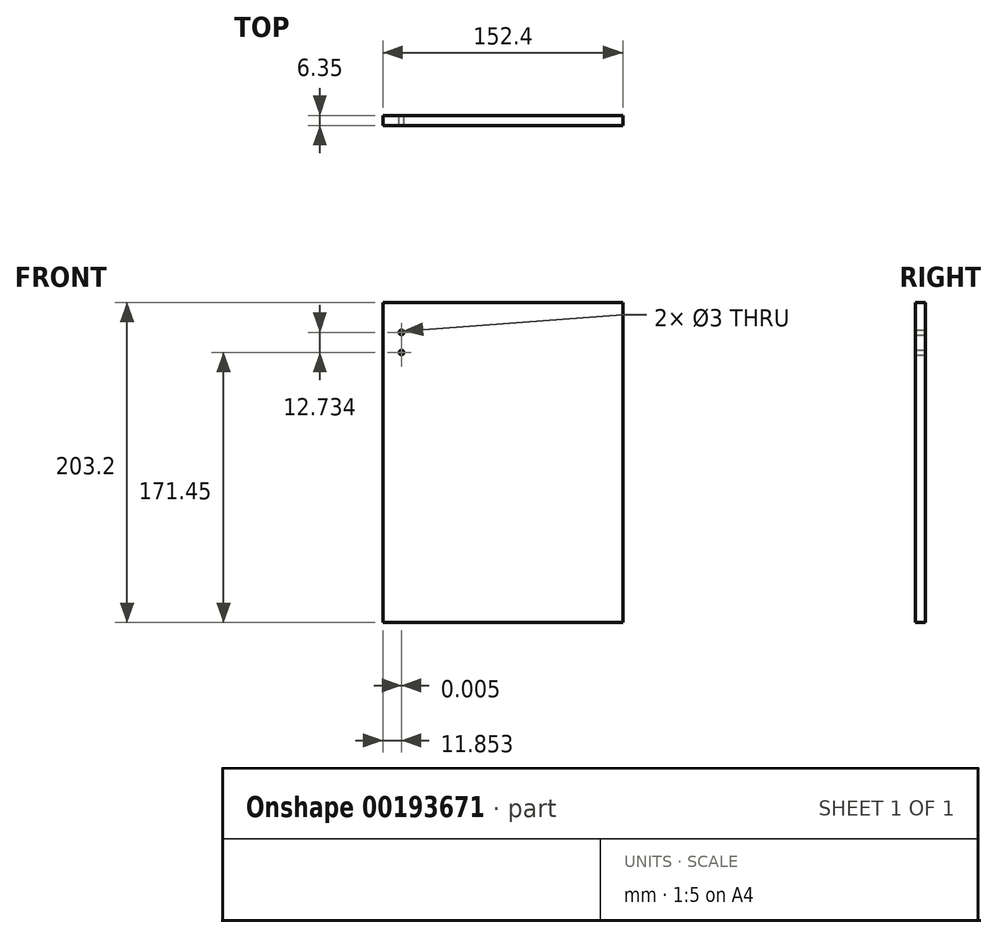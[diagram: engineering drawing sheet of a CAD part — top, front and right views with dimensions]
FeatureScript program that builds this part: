
annotation { "Feature Type Name" : "Feature", "Feature Type Description" : "" }
export const myFeature = defineFeature(function(context is Context, id is Id, definition is map)
    precondition{}
    {
        {
            var Q0;
            Q0=qCreatedBy(makeId("Front.planeOp"),FACE);
            var sketch = newSketch(context, id + "F0", { "sketchPlane" : qUnion([Q0])});
            skLineSegment(sketch, "E0.bottom", {"start": v(76.2, -101.6) * mm, "end": v(-76.2, -101.6) * mm});
            skLineSegment(sketch, "E0.top", {"start": v(76.2, 101.6) * mm, "end": v(-76.2, 101.6) * mm});
            skLineSegment(sketch, "E0.left", {"start": v(76.2, -101.6) * mm, "end": v(76.2, 101.6) * mm});
            skLineSegment(sketch, "E0.right", {"start": v(-76.2, -101.6) * mm, "end": v(-76.2, 101.6) * mm});
            skPoint(sketch, "E0.middle", {"position": v(0, 0) * mm});
            skSolve(sketch);
        }
        {
            var Q0;
            Q0=makeQuery(id+"F0.imprint","IMPRINT",FACE,{"disambiguationData":[TD([[makeQuery(id+"F0.imprint","IMPRINT",EDGE,{"derivedFrom":sQuery(id+"F0.wireOp",EDGE,"E0.bottom")}),-1.0]])]});
            extrude(context, id + "F1", {"entities" : qUnion([Q0]), "depth" : 6.35 * mm});
        }
        {
            var Q0;
            Q0=qCreatedBy(makeId("Front.planeOp"),FACE);
            var sketch = newSketch(context, id + "F2", { "sketchPlane" : qUnion([Q0])});
            skLineSegment(sketch, "E1", {"start": v(-64.35, 101.6) * mm, "end": v(-64.35, 82.55) * mm});
            skLineSegment(sketch, "E2", {"start": v(-64.35, 82.55) * mm, "end": v(-64.35, 69.85) * mm});
            skCircle(sketch, "E3", {"center": v(-64.35, 69.85) * mm, "radius": 1.5 * mm});
            skSolve(sketch);
        }
        {
            var Q0;
            Q0=qCreatedBy(makeId("Front.planeOp"),FACE);
            var sketch = newSketch(context, id + "F3", { "sketchPlane" : qUnion([Q0])});
            skCircle(sketch, "E4", {"center": v(-64.34, 82.58) * mm, "radius": 1.5 * mm});
            skSolve(sketch);
        }
        {
            var Q0;
            Q0=makeQuery(id+"F2.imprint","IMPRINT",FACE,{"disambiguationData":[TD([[makeQuery(id+"F2.imprint","IMPRINT",EDGE,{"derivedFrom":sQuery(id+"F2.wireOp",EDGE,"E3")}),1.0]])]});
            var Q1;
            Q1=makeQuery(id+"F3.imprint","IMPRINT",FACE,{"disambiguationData":[TD([[makeQuery(id+"F3.imprint","IMPRINT",EDGE,{"derivedFrom":sQuery(id+"F3.wireOp",EDGE,"E4")}),1.0]])]});
            var Q2;
            Q2=sQuery(id+"F2.wireOp",EDGE,"E3");
            var Q3;
            Q3=sQuery(id+"F3.wireOp",EDGE,"E4");
            extrude(context, id + "F4", {"entities" : qUnion([Q0, Q1]), "operationType" : NewBodyOperationType.REMOVE, "surfaceEntities" : qUnion([Q2, Q3]), "depth" : 25 * mm});
        }
    });
